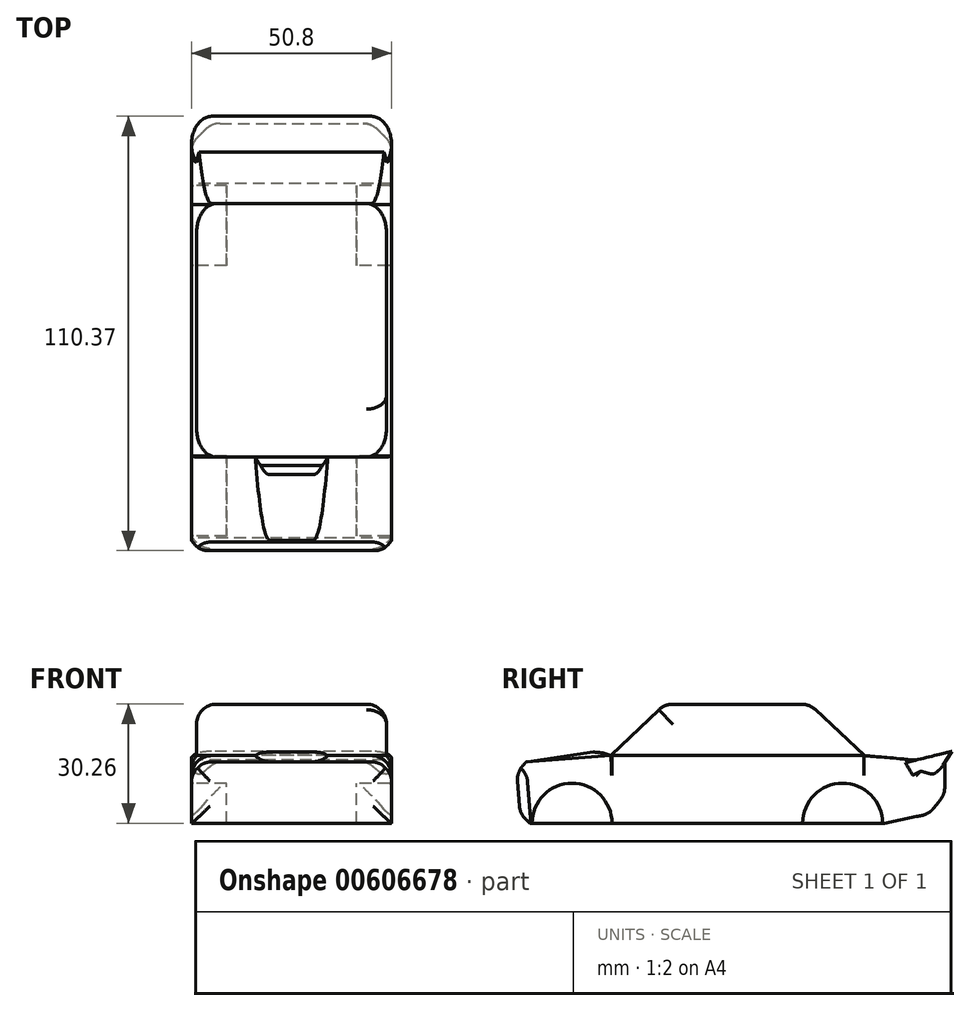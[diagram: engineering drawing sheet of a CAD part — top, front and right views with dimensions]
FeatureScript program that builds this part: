
annotation { "Feature Type Name" : "Feature", "Feature Type Description" : "" }
export const myFeature = defineFeature(function(context is Context, id is Id, definition is map)
    precondition{}
    {
        {
            var Q0;
            Q0=qCreatedBy(makeId("Right.planeOp"),FACE);
            var sketch = newSketch(context, id + "F0", { "sketchPlane" : qUnion([Q0])});
            skLineSegment(sketch, "E0", {"start": v(-44.17, -15.4) * mm, "end": v(38.94, -15.4) * mm});
            skLineSegment(sketch, "E1", {"start": v(38.94, -15.4) * mm, "end": v(54.25, -12.23) * mm});
            skLineSegment(sketch, "E2", {"start": v(54.25, -12.23) * mm, "end": v(54.25, 0) * mm});
            skLineSegment(sketch, "E3", {"start": v(54.25, 0) * mm, "end": v(33.9, 1.77) * mm});
            skLineSegment(sketch, "E4", {"start": v(33.9, 1.77) * mm, "end": v(19.89, 14.85) * mm});
            skLineSegment(sketch, "E5", {"start": v(19.89, 14.85) * mm, "end": v(-16.9, 14.85) * mm});
            skLineSegment(sketch, "E6", {"start": v(-16.9, 14.85) * mm, "end": v(-30.53, 1.77) * mm});
            skLineSegment(sketch, "E7", {"start": v(-30.53, 1.77) * mm, "end": v(-54.62, 0) * mm});
            skLineSegment(sketch, "E8", {"start": v(-54.62, 0) * mm, "end": v(-53.49, -15.4) * mm});
            skLineSegment(sketch, "E9", {"start": v(-53.49, -15.4) * mm, "end": v(-44.17, -15.4) * mm});
            skCircle(sketch, "E10", {"center": v(-40.43, -15.4) * mm, "radius": 10.16 * mm});
            skCircle(sketch, "E11", {"center": v(28.3, -15.4) * mm, "radius": 10.16 * mm});
            skLineSegment(sketch, "E12", {"start": v(46.94, 0.64) * mm, "end": v(56.07, 2.86) * mm});
            skLineSegment(sketch, "E13", {"start": v(54.25, 0) * mm, "end": v(56.07, 2.86) * mm});
            skLineSegment(sketch, "E14", {"start": v(-51.7, 0.22) * mm, "end": v(-33.8, 2.86) * mm});
            skLineSegment(sketch, "E15", {"start": v(-33.8, 2.86) * mm, "end": v(-30.53, 1.77) * mm});
            skLineSegment(sketch, "E16", {"start": v(-30.53, 1.77) * mm, "end": v(33.9, 1.77) * mm});
            skSolve(sketch);
        }
        {
            var Q0;
            {var subQ12=sQuery(id+"F0.wireOp",EDGE,"E1");Q0=makeQuery(id+"F0.imprint","IMPRINT",FACE,{"disambiguationData":[TD([[makeQuery(id+"F0.imprint","IMPRINT",EDGE,{"derivedFrom":subQ12}),1.0]])]});}
            extrude(context, id + "F1", {"entities" : qUnion([Q0]), "endBound" : BoundingType.SYMMETRIC, "depth" : 50.8 * mm, "offsetDistance" : 25.4 * mm});
        }
        {
            var Q0;
            {var subQ2=sQuery(id+"F0.wireOp",EDGE,"E12");Q0=makeQuery(id+"F0.imprint","IMPRINT",FACE,{"disambiguationData":[TD([[makeQuery(id+"F0.imprint","IMPRINT",EDGE,{"derivedFrom":subQ2}),-1.0]])]});}
            extrude(context, id + "F2", {"entities" : qUnion([Q0]), "operationType" : NewBodyOperationType.ADD, "endBound" : BoundingType.SYMMETRIC, "depth" : 50.8 * mm, "offsetDistance" : 25.4 * mm});
        }
        {
            var Q0;
            Q0=makeQuery(id+"F0.imprint","IMPRINT",FACE,{"disambiguationData":[TD([[makeQuery(id+"F0.imprint","IMPRINT",EDGE,{"derivedFrom":sQuery(id+"F0.wireOp",EDGE,"E4")}),1.0]])]});
            extrude(context, id + "F3", {"entities" : qUnion([Q0]), "operationType" : NewBodyOperationType.ADD, "endBound" : BoundingType.SYMMETRIC, "depth" : 48.26 * mm, "offsetDistance" : 25.4 * mm});
        }
        {
            var Q0;
            {var subQ2=sQuery(id+"F0.wireOp",EDGE,"E14");Q0=makeQuery(id+"F0.imprint","IMPRINT",FACE,{"disambiguationData":[TD([[makeQuery(id+"F0.imprint","IMPRINT",EDGE,{"derivedFrom":subQ2}),-1.0]])]});}
            extrude(context, id + "F4", {"entities" : qUnion([Q0]), "operationType" : NewBodyOperationType.ADD, "endBound" : BoundingType.SYMMETRIC, "depth" : 25.4 * mm, "offsetDistance" : 25.4 * mm});
        }
        {
            var Q0;
            {var subQ0=sQuery(id+"F0.wireOp",EDGE,"E10");var subQ1=sQuery(id+"F0.wireOp",EDGE,"E0");var subQ2=makeQuery(id+"F0.imprint","INTERSECT",VERTEX,{"derivedFrom":[subQ1,subQ0]});Q0=makeQuery(id+"F0.imprint","IMPRINT",FACE,{"disambiguationData":[TD([[makeQuery(id+"F0.imprint","IMPRINT",EDGE,{"disambiguationData":[TD([[subQ2,1.0]])],"derivedFrom":subQ1}),1.0]])]});}
            var Q1;
            {var subQ0=sQuery(id+"F0.wireOp",EDGE,"E11");var subQ1=sQuery(id+"F0.wireOp",EDGE,"E0");var subQ2=makeQuery(id+"F0.imprint","INTERSECT",VERTEX,{"disambiguationData":[OD(0.0)],"derivedFrom":[subQ1,subQ0]});Q1=makeQuery(id+"F0.imprint","IMPRINT",FACE,{"disambiguationData":[TD([[makeQuery(id+"F0.imprint","IMPRINT",EDGE,{"disambiguationData":[TD([[subQ2,-1.0]])],"derivedFrom":subQ1}),1.0]])]});}
            extrude(context, id + "F5", {"entities" : qUnion([Q0, Q1]), "operationType" : NewBodyOperationType.ADD, "endBound" : BoundingType.SYMMETRIC, "depth" : 33.02 * mm, "offsetDistance" : 25.4 * mm});
        }
        {
            var Q0;
            Q0=makeQuery(id+"F4.opExtrude","CAP_EDGE",EDGE,{"disambiguationData":[OSD([sQuery(id+"F0.wireOp",EDGE,"E14")])],"isStart":false});
            var Q1;
            Q1=makeQuery(id+"F4.opExtrude","CAP_EDGE",EDGE,{"disambiguationData":[OSD([sQuery(id+"F0.wireOp",EDGE,"E14")])],"isStart":true});
            var Q2;
            Q2=makeQuery(id+"F4.opExtrude","SWEPT_EDGE",EDGE,{"disambiguationData":[OSD([sQuery(id+"F0.wireOp",EDGE,"E14"),sQuery(id+"F0.wireOp",EDGE,"E15")])]});
            chamfer(context, id + "F6", {"entities" : qUnion([Q0, Q1, Q2]), "width" : 5.08 * mm, "tangentPropagation" : true});
        }
        {
            var Q0;
            Q0=makeQuery(id+"F3.opExtrude","SWEPT_EDGE",EDGE,{"disambiguationData":[OSD([sQuery(id+"F0.wireOp",EDGE,"E5"),sQuery(id+"F0.wireOp",EDGE,"E6")])]});
            var Q1;
            Q1=makeQuery(id+"F3.opExtrude","SWEPT_EDGE",EDGE,{"disambiguationData":[OSD([sQuery(id+"F0.wireOp",EDGE,"E4"),sQuery(id+"F0.wireOp",EDGE,"E5")])]});
            var Q2;
            Q2=makeQuery(id+"F3.opExtrude","CAP_EDGE",EDGE,{"disambiguationData":[OSD([sQuery(id+"F0.wireOp",EDGE,"E4")])],"isStart":false});
            var Q3;
            Q3=makeQuery(id+"F3.opExtrude","CAP_EDGE",EDGE,{"disambiguationData":[OSD([sQuery(id+"F0.wireOp",EDGE,"E4")])],"isStart":true});
            var Q4;
            Q4=makeQuery(id+"F3.opExtrude","CAP_EDGE",EDGE,{"disambiguationData":[OSD([sQuery(id+"F0.wireOp",EDGE,"E6")])],"isStart":false});
            var Q5;
            Q5=makeQuery(id+"F3.opExtrude","CAP_EDGE",EDGE,{"disambiguationData":[OSD([sQuery(id+"F0.wireOp",EDGE,"E6")])],"isStart":true});
            var Q6;
            Q6=makeQuery(id+"F3.opExtrude","CAP_EDGE",EDGE,{"disambiguationData":[OSD([sQuery(id+"F0.wireOp",EDGE,"E5")])],"isStart":false});
            var Q7;
            Q7=makeQuery(id+"F3.opExtrude","CAP_EDGE",EDGE,{"disambiguationData":[OSD([sQuery(id+"F0.wireOp",EDGE,"E5")])],"isStart":true});
            fillet(context, id + "F7", {"entities" : qUnion([Q0, Q1, Q2, Q3, Q4, Q5, Q6, Q7]), "tangentPropagation" : true, "radius" : 5.08 * mm, "defaultsChanged" : false, "vertexSettings" : [], "allowEdgeOverflow" : false});
        }
        {
            var Q0;
            Q0=makeQuery(id+"F1.opExtrude","CAP_EDGE",EDGE,{"disambiguationData":[OSD([sQuery(id+"F0.wireOp",EDGE,"E10")])],"isStart":false});
            var Q1;
            Q1=makeQuery(id+"F1.opExtrude","CAP_EDGE",EDGE,{"disambiguationData":[OSD([sQuery(id+"F0.wireOp",EDGE,"E11")])],"isStart":false});
            var Q2;
            Q2=makeQuery(id+"F1.opExtrude","CAP_EDGE",EDGE,{"disambiguationData":[OSD([sQuery(id+"F0.wireOp",EDGE,"E10")])],"isStart":true});
            var Q3;
            Q3=makeQuery(id+"F1.opExtrude","CAP_EDGE",EDGE,{"disambiguationData":[OSD([sQuery(id+"F0.wireOp",EDGE,"E11")])],"isStart":true});
            fillet(context, id + "F8", {"entities" : qUnion([Q0, Q1, Q2, Q3]), "tangentPropagation" : true, "radius" : 0.5 * mm, "defaultsChanged" : true, "vertexSettings" : [], "allowEdgeOverflow" : false});
        }
        {
            var Q0;
            Q0=makeQuery(id+"F1.opExtrude","CAP_EDGE",EDGE,{"disambiguationData":[OSD([sQuery(id+"F0.wireOp",EDGE,"E2")])],"isStart":false});
            var Q1;
            Q1=makeQuery(id+"F1.opExtrude","CAP_EDGE",EDGE,{"disambiguationData":[OSD([sQuery(id+"F0.wireOp",EDGE,"E2")])],"isStart":true});
            var Q2;
            Q2=makeQuery(id+"F1.opExtrude","SWEPT_EDGE",EDGE,{"disambiguationData":[OSD([sQuery(id+"F0.wireOp",EDGE,"E1"),sQuery(id+"F0.wireOp",EDGE,"E2")])]});
            chamfer(context, id + "F9", {"entities" : qUnion([Q0, Q1, Q2]), "width" : 5.08 * mm, "tangentPropagation" : true});
        }
        {
            var Q0;
            {var subQ0=sQuery(id+"F0.wireOp",EDGE,"E1");Q0=makeQuery(id+"F9.opChamfer","BLEND_EDGE",EDGE,{"blendedFrom":[makeQuery(id+"F1.opExtrude","SWEPT_EDGE",EDGE,{"disambiguationData":[OSD([subQ0,sQuery(id+"F0.wireOp",EDGE,"E2")])]}),makeQuery(id+"F1.opExtrude","SWEPT_FACE",FACE,{"disambiguationData":[OSD([subQ0])]})],"blendedInto":[makeQuery(id+"F1.opExtrude","SWEPT_FACE",FACE,{"disambiguationData":[OSD([subQ0])]})]});}
            var Q1;
            {var subQ0=sQuery(id+"F0.wireOp",EDGE,"E2");Q1=makeQuery(id+"F9.opChamfer","BLEND_EDGE",EDGE,{"blendedFrom":[makeQuery(id+"F1.opExtrude","SWEPT_EDGE",EDGE,{"disambiguationData":[OSD([sQuery(id+"F0.wireOp",EDGE,"E1"),subQ0])]}),makeQuery(id+"F1.opExtrude","SWEPT_FACE",FACE,{"disambiguationData":[OSD([subQ0])]})],"blendedInto":[makeQuery(id+"F1.opExtrude","SWEPT_FACE",FACE,{"disambiguationData":[OSD([subQ0])]})]});}
            var Q2;
            {var subQ0=sQuery(id+"F0.wireOp",EDGE,"E2");Q2=makeQuery(id+"F9.opChamfer","BLEND_EDGE",EDGE,{"blendedFrom":[makeQuery(id+"F1.opExtrude","CAP_EDGE",EDGE,{"disambiguationData":[OSD([subQ0])],"isStart":false}),makeQuery(id+"F1.opExtrude","SWEPT_FACE",FACE,{"disambiguationData":[OSD([subQ0])]})],"blendedInto":[makeQuery(id+"F1.opExtrude","SWEPT_FACE",FACE,{"disambiguationData":[OSD([subQ0])]})]});}
            var Q3;
            {var subQ0=sQuery(id+"F0.wireOp",EDGE,"E3");var subQ1=sQuery(id+"F0.wireOp",EDGE,"E2");Q3=makeQuery(id+"F9.opChamfer","BLEND_EDGE",EDGE,{"blendedFrom":[makeQuery(id+"F1.opExtrude","CAP_EDGE",EDGE,{"disambiguationData":[OSD([subQ1])],"isStart":false}),makeQuery(id+"F2.boolean.opBoolean","MERGE",FACE,{"derivedFrom":[makeQuery(id+"F1.opExtrude","CAP_FACE",FACE,{"disambiguationData":[OSD([sQuery(id+"F0.wireOp",EDGE,"E0"),sQuery(id+"F0.wireOp",EDGE,"E1"),subQ1,subQ0,sQuery(id+"F0.wireOp",EDGE,"E7"),sQuery(id+"F0.wireOp",EDGE,"E8"),sQuery(id+"F0.wireOp",EDGE,"E9"),sQuery(id+"F0.wireOp",EDGE,"E10"),sQuery(id+"F0.wireOp",EDGE,"E11"),sQuery(id+"F0.wireOp",EDGE,"E16")])],"isStart":false}),makeQuery(id+"F2.opExtrude","CAP_FACE",FACE,{"disambiguationData":[OSD([subQ0,sQuery(id+"F0.wireOp",EDGE,"E12"),sQuery(id+"F0.wireOp",EDGE,"E13")])],"isStart":false})]})],"blendedInto":[makeQuery(id+"F2.boolean.opBoolean","MERGE",FACE,{"derivedFrom":[makeQuery(id+"F1.opExtrude","CAP_FACE",FACE,{"disambiguationData":[OSD([sQuery(id+"F0.wireOp",EDGE,"E0"),sQuery(id+"F0.wireOp",EDGE,"E1"),subQ1,subQ0,sQuery(id+"F0.wireOp",EDGE,"E7"),sQuery(id+"F0.wireOp",EDGE,"E8"),sQuery(id+"F0.wireOp",EDGE,"E9"),sQuery(id+"F0.wireOp",EDGE,"E10"),sQuery(id+"F0.wireOp",EDGE,"E11"),sQuery(id+"F0.wireOp",EDGE,"E16")])],"isStart":false}),makeQuery(id+"F2.opExtrude","CAP_FACE",FACE,{"disambiguationData":[OSD([subQ0,sQuery(id+"F0.wireOp",EDGE,"E12"),sQuery(id+"F0.wireOp",EDGE,"E13")])],"isStart":false})]})]});}
            var Q4;
            {var subQ0=sQuery(id+"F0.wireOp",EDGE,"E3");var subQ1=sQuery(id+"F0.wireOp",EDGE,"E2");Q4=makeQuery(id+"F9.opChamfer","BLEND_EDGE",EDGE,{"blendedFrom":[makeQuery(id+"F1.opExtrude","CAP_EDGE",EDGE,{"disambiguationData":[OSD([subQ1])],"isStart":true}),makeQuery(id+"F2.boolean.opBoolean","MERGE",FACE,{"derivedFrom":[makeQuery(id+"F1.opExtrude","CAP_FACE",FACE,{"disambiguationData":[OSD([sQuery(id+"F0.wireOp",EDGE,"E0"),sQuery(id+"F0.wireOp",EDGE,"E1"),subQ1,subQ0,sQuery(id+"F0.wireOp",EDGE,"E7"),sQuery(id+"F0.wireOp",EDGE,"E8"),sQuery(id+"F0.wireOp",EDGE,"E9"),sQuery(id+"F0.wireOp",EDGE,"E10"),sQuery(id+"F0.wireOp",EDGE,"E11"),sQuery(id+"F0.wireOp",EDGE,"E16")])],"isStart":true}),makeQuery(id+"F2.opExtrude","CAP_FACE",FACE,{"disambiguationData":[OSD([subQ0,sQuery(id+"F0.wireOp",EDGE,"E12"),sQuery(id+"F0.wireOp",EDGE,"E13")])],"isStart":true})]})],"blendedInto":[makeQuery(id+"F2.boolean.opBoolean","MERGE",FACE,{"derivedFrom":[makeQuery(id+"F1.opExtrude","CAP_FACE",FACE,{"disambiguationData":[OSD([sQuery(id+"F0.wireOp",EDGE,"E0"),sQuery(id+"F0.wireOp",EDGE,"E1"),subQ1,subQ0,sQuery(id+"F0.wireOp",EDGE,"E7"),sQuery(id+"F0.wireOp",EDGE,"E8"),sQuery(id+"F0.wireOp",EDGE,"E9"),sQuery(id+"F0.wireOp",EDGE,"E10"),sQuery(id+"F0.wireOp",EDGE,"E11"),sQuery(id+"F0.wireOp",EDGE,"E16")])],"isStart":true}),makeQuery(id+"F2.opExtrude","CAP_FACE",FACE,{"disambiguationData":[OSD([subQ0,sQuery(id+"F0.wireOp",EDGE,"E12"),sQuery(id+"F0.wireOp",EDGE,"E13")])],"isStart":true})]})]});}
            var Q5;
            {var subQ0=sQuery(id+"F0.wireOp",EDGE,"E2");Q5=makeQuery(id+"F9.opChamfer","BLEND_EDGE",EDGE,{"blendedFrom":[makeQuery(id+"F1.opExtrude","CAP_EDGE",EDGE,{"disambiguationData":[OSD([subQ0])],"isStart":true}),makeQuery(id+"F1.opExtrude","SWEPT_FACE",FACE,{"disambiguationData":[OSD([subQ0])]})],"blendedInto":[makeQuery(id+"F1.opExtrude","SWEPT_FACE",FACE,{"disambiguationData":[OSD([subQ0])]})]});}
            fillet(context, id + "F10", {"entities" : qUnion([Q0, Q1, Q2, Q3, Q4, Q5]), "tangentPropagation" : true, "radius" : 5.08 * mm, "defaultsChanged" : false, "vertexSettings" : [], "allowEdgeOverflow" : false});
        }
        {
            var Q0;
            Q0=makeQuery(id+"F2.opExtrude","CAP_EDGE",EDGE,{"disambiguationData":[OSD([sQuery(id+"F0.wireOp",EDGE,"E13")])],"isStart":false});
            var Q1;
            Q1=makeQuery(id+"F2.opExtrude","CAP_EDGE",EDGE,{"disambiguationData":[OSD([sQuery(id+"F0.wireOp",EDGE,"E13")])],"isStart":true});
            fillet(context, id + "F11", {"entities" : qUnion([Q0, Q1]), "tangentPropagation" : true, "radius" : 5.08 * mm, "defaultsChanged" : false, "vertexSettings" : [], "allowEdgeOverflow" : false});
        }
        {
            var Q0;
            Q0=makeQuery(id+"F1.opExtrude","CAP_EDGE",EDGE,{"disambiguationData":[OSD([sQuery(id+"F0.wireOp",EDGE,"E8")])],"isStart":true});
            var Q1;
            Q1=makeQuery(id+"F1.opExtrude","CAP_EDGE",EDGE,{"disambiguationData":[OSD([sQuery(id+"F0.wireOp",EDGE,"E8")])],"isStart":false});
            var Q2;
            Q2=makeQuery(id+"F1.opExtrude","SWEPT_EDGE",EDGE,{"disambiguationData":[OSD([sQuery(id+"F0.wireOp",EDGE,"E7"),sQuery(id+"F0.wireOp",EDGE,"E8")])]});
            var Q3;
            Q3=makeQuery(id+"F1.opExtrude","SWEPT_EDGE",EDGE,{"disambiguationData":[OSD([sQuery(id+"F0.wireOp",EDGE,"E8"),sQuery(id+"F0.wireOp",EDGE,"E9")])]});
            chamfer(context, id + "F12", {"entities" : qUnion([Q0, Q1, Q2, Q3]), "width" : 2.54 * mm, "tangentPropagation" : true});
        }
        {
            var Q0;
            {var subQ0=sQuery(id+"F0.wireOp",EDGE,"E8");Q0=makeQuery(id+"F12.opChamfer","BLEND_EDGE",EDGE,{"blendedFrom":[makeQuery(id+"F1.opExtrude","SWEPT_EDGE",EDGE,{"disambiguationData":[OSD([sQuery(id+"F0.wireOp",EDGE,"E7"),subQ0])]}),makeQuery(id+"F1.opExtrude","SWEPT_FACE",FACE,{"disambiguationData":[OSD([subQ0])]})],"blendedInto":[makeQuery(id+"F1.opExtrude","SWEPT_FACE",FACE,{"disambiguationData":[OSD([subQ0])]})]});}
            var Q1;
            {var subQ0=sQuery(id+"F0.wireOp",EDGE,"E8");Q1=makeQuery(id+"F12.opChamfer","BLEND_EDGE",EDGE,{"blendedFrom":[makeQuery(id+"F1.opExtrude","CAP_EDGE",EDGE,{"disambiguationData":[OSD([subQ0])],"isStart":true}),makeQuery(id+"F1.opExtrude","SWEPT_FACE",FACE,{"disambiguationData":[OSD([subQ0])]})],"blendedInto":[makeQuery(id+"F1.opExtrude","SWEPT_FACE",FACE,{"disambiguationData":[OSD([subQ0])]})]});}
            var Q2;
            {var subQ0=sQuery(id+"F0.wireOp",EDGE,"E8");Q2=makeQuery(id+"F12.opChamfer","BLEND_EDGE",EDGE,{"blendedFrom":[makeQuery(id+"F1.opExtrude","SWEPT_EDGE",EDGE,{"disambiguationData":[OSD([subQ0,sQuery(id+"F0.wireOp",EDGE,"E9")])]}),makeQuery(id+"F1.opExtrude","SWEPT_FACE",FACE,{"disambiguationData":[OSD([subQ0])]})],"blendedInto":[makeQuery(id+"F1.opExtrude","SWEPT_FACE",FACE,{"disambiguationData":[OSD([subQ0])]})]});}
            var Q3;
            {var subQ0=sQuery(id+"F0.wireOp",EDGE,"E8");Q3=makeQuery(id+"F12.opChamfer","BLEND_EDGE",EDGE,{"blendedFrom":[makeQuery(id+"F1.opExtrude","CAP_EDGE",EDGE,{"disambiguationData":[OSD([subQ0])],"isStart":false}),makeQuery(id+"F1.opExtrude","SWEPT_FACE",FACE,{"disambiguationData":[OSD([subQ0])]})],"blendedInto":[makeQuery(id+"F1.opExtrude","SWEPT_FACE",FACE,{"disambiguationData":[OSD([subQ0])]})]});}
            fillet(context, id + "F13", {"entities" : qUnion([Q0, Q1, Q2, Q3]), "tangentPropagation" : true, "radius" : 5.08 * mm, "defaultsChanged" : false, "vertexSettings" : [], "allowEdgeOverflow" : false});
        }
        {
            var Q0;
            {var subQ0=sQuery(id+"F0.wireOp",EDGE,"E14");Q0=makeQuery(id+"F6.opChamfer","BLEND_EDGE",EDGE,{"blendedFrom":[makeQuery(id+"F4.opExtrude","CAP_EDGE",EDGE,{"disambiguationData":[OSD([subQ0])],"isStart":false}),makeQuery(id+"F4.opExtrude","SWEPT_FACE",FACE,{"disambiguationData":[OSD([subQ0])]})],"blendedInto":[makeQuery(id+"F4.opExtrude","SWEPT_FACE",FACE,{"disambiguationData":[OSD([subQ0])]})]});}
            var Q1;
            {var subQ0=sQuery(id+"F0.wireOp",EDGE,"E14");Q1=makeQuery(id+"F6.opChamfer","BLEND_EDGE",EDGE,{"blendedFrom":[makeQuery(id+"F4.opExtrude","CAP_EDGE",EDGE,{"disambiguationData":[OSD([subQ0])],"isStart":true}),makeQuery(id+"F4.opExtrude","SWEPT_FACE",FACE,{"disambiguationData":[OSD([subQ0])]})],"blendedInto":[makeQuery(id+"F4.opExtrude","SWEPT_FACE",FACE,{"disambiguationData":[OSD([subQ0])]})]});}
            fillet(context, id + "F14", {"entities" : qUnion([Q0, Q1]), "tangentPropagation" : true, "radius" : 5.08 * mm, "defaultsChanged" : false, "vertexSettings" : [], "allowEdgeOverflow" : false});
        }
        {
            var Q0;
            Q0=makeQuery(id+"F1.opExtrude","CAP_EDGE",EDGE,{"disambiguationData":[OSD([sQuery(id+"F0.wireOp",EDGE,"E7")])],"isStart":false});
            var Q1;
            Q1=makeQuery(id+"F1.opExtrude","CAP_EDGE",EDGE,{"disambiguationData":[OSD([sQuery(id+"F0.wireOp",EDGE,"E16")])],"isStart":false});
            var Q2;
            Q2=makeQuery(id+"F1.opExtrude","CAP_EDGE",EDGE,{"disambiguationData":[OSD([sQuery(id+"F0.wireOp",EDGE,"E7")])],"isStart":true});
            var Q3;
            Q3=makeQuery(id+"F1.opExtrude","CAP_EDGE",EDGE,{"disambiguationData":[OSD([sQuery(id+"F0.wireOp",EDGE,"E16")])],"isStart":true});
            fillet(context, id + "F15", {"entities" : qUnion([Q0, Q1, Q2, Q3]), "tangentPropagation" : true, "radius" : 5.08 * mm, "defaultsChanged" : false, "vertexSettings" : [], "allowEdgeOverflow" : false});
        }
    });
